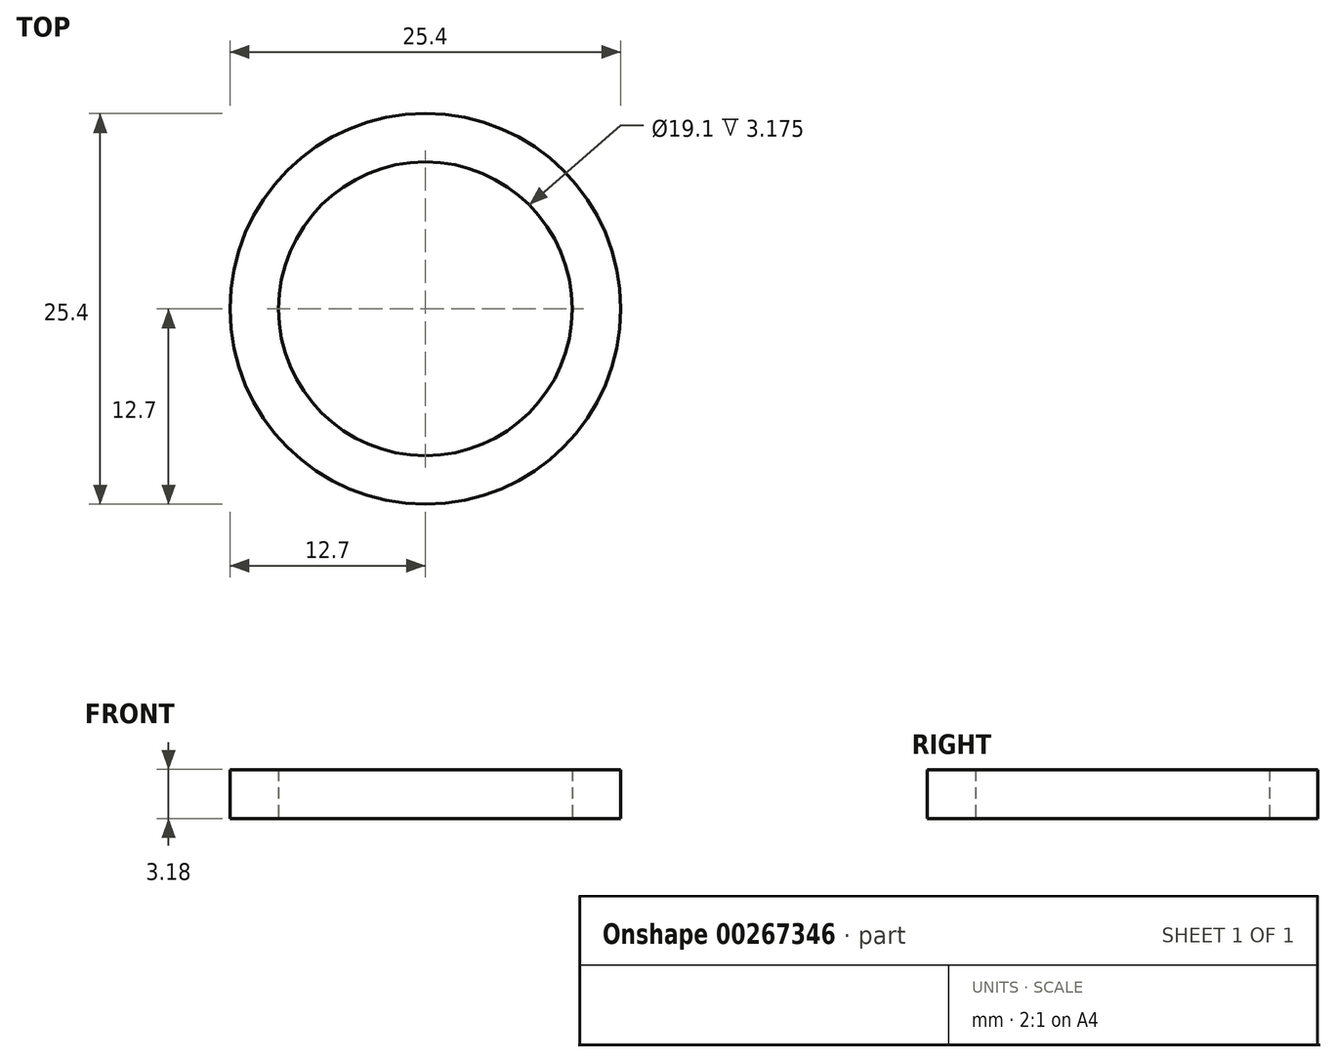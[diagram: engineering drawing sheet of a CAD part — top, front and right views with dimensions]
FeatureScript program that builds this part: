
annotation { "Feature Type Name" : "Feature", "Feature Type Description" : "" }
export const myFeature = defineFeature(function(context is Context, id is Id, definition is map)
    precondition{}
    {
        {
            var Q0;
            Q0=qCreatedBy(makeId("Top.planeOp"),FACE);
            var sketch = newSketch(context, id + "F0", { "sketchPlane" : qUnion([Q0])});
            skCircle(sketch, "E0", {"center": v(0, 0) * mm, "radius": 9.55 * mm});
            skCircle(sketch, "E1", {"center": v(0, 0) * mm, "radius": 12.7 * mm});
            skSolve(sketch);
        }
        {
            var Q0;
            Q0 = qSketchRegion(id + "F0", true);
            extrude(context, id + "F1", {"entities" : qUnion([Q0]), "depth" : 3.17 * mm});
        }
    });
